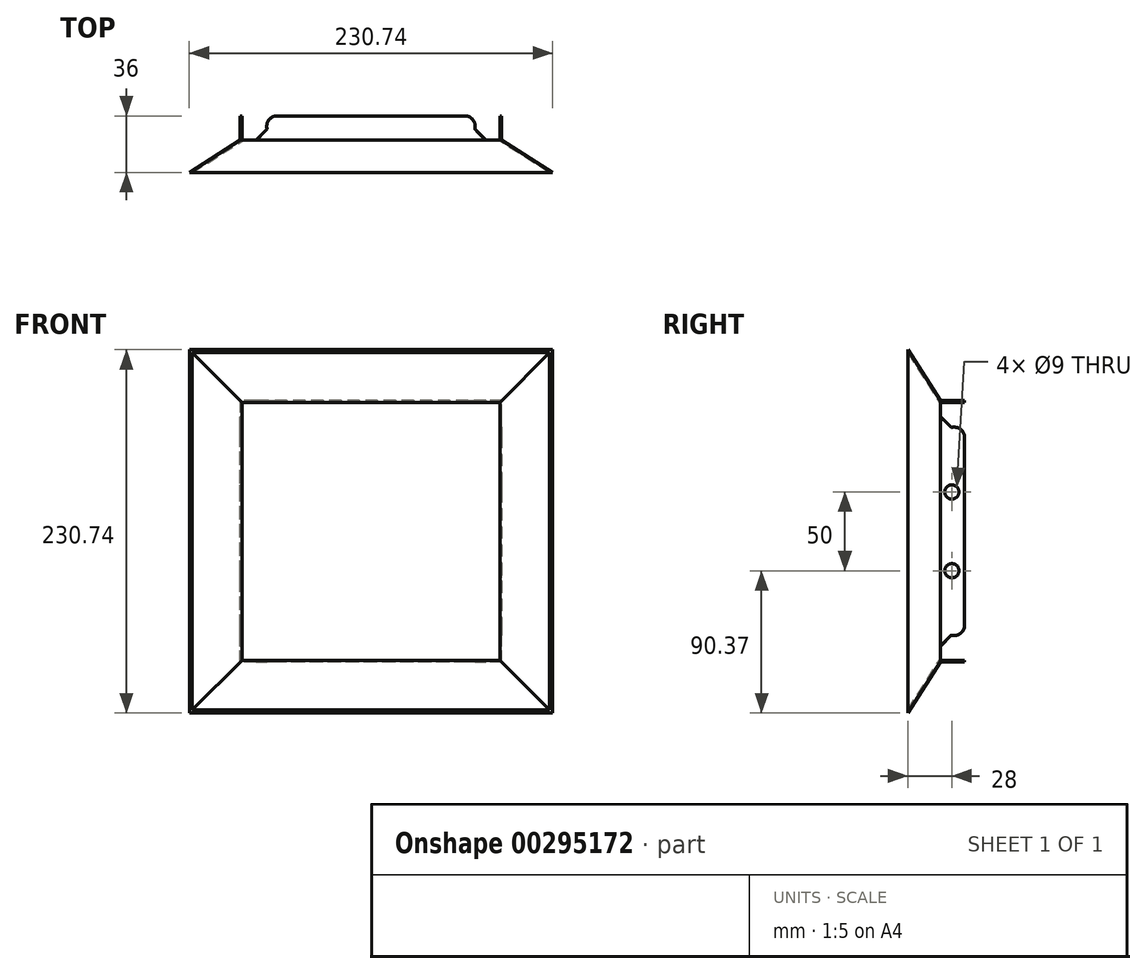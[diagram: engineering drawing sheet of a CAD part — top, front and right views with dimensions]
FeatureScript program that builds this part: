
annotation { "Feature Type Name" : "Feature", "Feature Type Description" : "" }
export const myFeature = defineFeature(function(context is Context, id is Id, definition is map)
    precondition{}
    {
        {
            var Q0;
            Q0=qCreatedBy(makeId("Front.planeOp"),FACE);
            var sketch = newSketch(context, id + "F0", { "sketchPlane" : qUnion([Q0])});
            skLineSegment(sketch, "E0.bottom", {"start": v(118.5, 118.5) * mm, "end": v(-118.5, 118.5) * mm});
            skLineSegment(sketch, "E0.top", {"start": v(118.5, -118.5) * mm, "end": v(-118.5, -118.5) * mm});
            skLineSegment(sketch, "E0.left", {"start": v(118.5, 118.5) * mm, "end": v(118.5, -118.5) * mm});
            skLineSegment(sketch, "E0.right", {"start": v(-118.5, 118.5) * mm, "end": v(-118.5, -118.5) * mm});
            skPoint(sketch, "E0.middle", {"position": v(0, 0) * mm});
            skLineSegment(sketch, "E1.bottom", {"start": v(-113.5, 113.5) * mm, "end": v(113.5, 113.5) * mm});
            skLineSegment(sketch, "E1.top", {"start": v(-113.5, -113.5) * mm, "end": v(113.5, -113.5) * mm});
            skLineSegment(sketch, "E1.left", {"start": v(-113.5, 113.5) * mm, "end": v(-113.5, -113.5) * mm});
            skLineSegment(sketch, "E1.right", {"start": v(113.5, 113.5) * mm, "end": v(113.5, -113.5) * mm});
            skSolve(sketch);
        }
        {
            var Q0;
            Q0=qCreatedBy(makeId("Front.planeOp"),FACE);
            cPlane(context, id + "F1", {"entities" : qUnion([Q0]), "cplaneType" : CPlaneType.OFFSET, "offset" : 20 * mm, "oppositeDirection" : true, "width" : 150 * mm, "height" : 150 * mm});
        }
        {
            var Q0;
            Q0=qCreatedBy(id+"F1.planeOp",FACE);
            var sketch = newSketch(context, id + "F2", { "sketchPlane" : qUnion([Q0])});
            skLineSegment(sketch, "E2.bottom", {"start": v(82, 82) * mm, "end": v(-82, 82) * mm});
            skLineSegment(sketch, "E2.top", {"start": v(82, -82) * mm, "end": v(-82, -82) * mm});
            skLineSegment(sketch, "E2.left", {"start": v(82, 82) * mm, "end": v(82, -82) * mm});
            skLineSegment(sketch, "E2.right", {"start": v(-82, 82) * mm, "end": v(-82, -82) * mm});
            skPoint(sketch, "E2.middle", {"position": v(0, 0) * mm});
            skSolve(sketch);
        }
        {
            var Q0;
            Q0=makeQuery(id+"F0.imprint","IMPRINT",FACE,{"disambiguationData":[TD([[makeQuery(id+"F0.imprint","IMPRINT",EDGE,{"derivedFrom":sQuery(id+"F0.wireOp",EDGE,"E1.bottom")}),-1.0]])]});
            var Q1;
            Q1=makeQuery(id+"F2.imprint","IMPRINT",FACE,{"disambiguationData":[TD([[makeQuery(id+"F2.imprint","IMPRINT",EDGE,{"derivedFrom":sQuery(id+"F2.wireOp",EDGE,"E2.bottom")}),1.0]])]});
            loft(context, id + "F3", {"sheetProfilesArray" : [{ "sheetProfileEntities" : qUnion([Q0]) }, { "sheetProfileEntities" : qUnion([Q1]) }]});
        }
        {
            var Q0;
            Q0=qCreatedBy(id+"F1.planeOp",FACE);
            cPlane(context, id + "F4", {"entities" : qUnion([Q0]), "cplaneType" : CPlaneType.OFFSET, "offset" : 16 * mm, "oppositeDirection" : true, "width" : 150 * mm, "height" : 150 * mm});
        }
        {
            var Q0;
            Q0=qCreatedBy(id+"F4.planeOp",FACE);
            var sketch = newSketch(context, id + "F5", { "sketchPlane" : qUnion([Q0])});
            skLineSegment(sketch, "E3.0.0", {"start": v(82, -82) * mm, "end": v(-82, -82) * mm});
            skLineSegment(sketch, "E3.0.1", {"start": v(-82, -82) * mm, "end": v(-82, 82) * mm});
            skLineSegment(sketch, "E3.0.2", {"start": v(-82, 82) * mm, "end": v(82, 82) * mm});
            skLineSegment(sketch, "E3.0.3", {"start": v(82, 82) * mm, "end": v(82, -82) * mm});
            skSolve(sketch);
        }
        {
            var Q1;
            Q1=makeQuery(id+"F5.imprint","IMPRINT",FACE,{"disambiguationData":[TD([[makeQuery(id+"F5.imprint","IMPRINT",EDGE,{"derivedFrom":sQuery(id+"F5.wireOp",EDGE,"E3.0.0")}),-1.0]])]});
            var Q2;
            Q2=makeQuery(id+"F3.opLoft","CAP_FACE",FACE,{"disambiguationData":[OSD([makeQuery(id+"F2.imprint","IMPRINT",FACE,{"disambiguationData":[TD([[makeQuery(id+"F2.imprint","IMPRINT",EDGE,{"derivedFrom":sQuery(id+"F2.wireOp",EDGE,"E2.bottom")}),1.0]])]})])],"isStart":true});
            loft(context, id + "F6", {"operationType" : NewBodyOperationType.ADD, "sheetProfilesArray" : [{ "sheetProfileEntities" : qUnion([Q1]) }, { "sheetProfileEntities" : qUnion([Q2]) }]});
        }
        {
            var Q0;
            Q0=makeQuery(id+"F3.opLoft","CAP_FACE",FACE,{"disambiguationData":[OSD([makeQuery(id+"F0.imprint","IMPRINT",FACE,{"disambiguationData":[TD([[makeQuery(id+"F0.imprint","IMPRINT",EDGE,{"derivedFrom":sQuery(id+"F0.wireOp",EDGE,"E1.bottom")}),-1.0]])]})])],"isStart":true});
            var Q1;
            Q1=makeQuery(id+"F6.opLoft","CAP_FACE",FACE,{"disambiguationData":[OSD([makeQuery(id+"F5.imprint","IMPRINT",FACE,{"disambiguationData":[TD([[makeQuery(id+"F5.imprint","IMPRINT",EDGE,{"derivedFrom":sQuery(id+"F5.wireOp",EDGE,"E3.0.0")}),-1.0]])]})])],"isStart":true});
            shell(context, id + "F7", {"entities" : qUnion([Q0, Q1]), "thickness" : 1 * mm, "oppositeDirection" : true});
        }
        {
            var Q0;
            Q0=makeQuery(id+"F6.opLoft","SWEPT_FACE",FACE,{"disambiguationData":[OSD([sQuery(id+"F2.wireOp",EDGE,"E2.bottom"),sQuery(id+"F2.wireOp",EDGE,"E2.top"),sQuery(id+"F2.wireOp",EDGE,"E2.right"),sQuery(id+"F5.wireOp",EDGE,"E3.0.0"),sQuery(id+"F5.wireOp",EDGE,"E3.0.1"),sQuery(id+"F5.wireOp",EDGE,"E3.0.2")])]});
            var sketch = newSketch(context, id + "F8", { "sketchPlane" : qUnion([Q0])});
            skLineSegment(sketch, "E4", {"start": v(-20.55, 83) * mm, "end": v(-20.55, 73) * mm});
            skLineSegment(sketch, "E5", {"start": v(-20.55, 73) * mm, "end": v(-27.62, 65.93) * mm});
            skArc(sketch, "E6", {"start": v(-27.62, 65.93) * mm, "mid": v(-33.79, 64.53) * mm, "end": v(-36, 58.6) * mm});
            skLineSegment(sketch, "E7", {"start": v(-20.55, 83) * mm, "end": v(-36, 83) * mm});
            skLineSegment(sketch, "E8", {"start": v(-36, 83) * mm, "end": v(-36, 58.6) * mm});
            skLineSegment(sketch, "E9.MirrorCS", {"start": v(-20.55, -83) * mm, "end": v(-36, -83) * mm});
            skArc(sketch, "E10.MirrorCS", {"start": v(-27.62, -65.93) * mm, "mid": v(-33.79, -64.53) * mm, "end": v(-36, -58.6) * mm});
            skLineSegment(sketch, "E11.MirrorCS", {"start": v(-20.55, -83) * mm, "end": v(-20.55, -73) * mm});
            skLineSegment(sketch, "E12.MirrorCS", {"start": v(-20.55, -73) * mm, "end": v(-27.62, -65.93) * mm});
            skLineSegment(sketch, "E13.MirrorCS", {"start": v(-36, -83) * mm, "end": v(-36, -58.6) * mm});
            skSolve(sketch);
        }
        {
            var Q0;
            Q0=makeQuery(id+"F8.imprint","IMPRINT",FACE,{"disambiguationData":[TD([[makeQuery(id+"F8.imprint","IMPRINT",EDGE,{"derivedFrom":sQuery(id+"F8.wireOp",EDGE,"E4")}),1.0]])]});
            var Q1;
            Q1=sQuery(id+"F8.wireOp",EDGE,"E7");
            revolve(context, id + "F9", {"operationType" : NewBodyOperationType.REMOVE, "entities" : qUnion([Q0]), "axis" : qUnion([Q1]), "revolveType" : RevolveType.FULL, "oppositeDirection" : true});
        }
        {
            var Q0;
            {var subQ4=sQuery(id+"F8.wireOp",EDGE,"E9.MirrorCS");Q0=makeQuery(id+"F8.imprint","IMPRINT",FACE,{"disambiguationData":[TD([[makeQuery(id+"F8.imprint","IMPRINT",EDGE,{"derivedFrom":subQ4}),1.0]])]});}
            var Q1;
            Q1=sQuery(id+"F8.wireOp",EDGE,"E9.MirrorCS");
            revolve(context, id + "F10", {"operationType" : NewBodyOperationType.REMOVE, "entities" : qUnion([Q0]), "axis" : qUnion([Q1]), "revolveType" : RevolveType.FULL, "oppositeDirection" : true});
        }
        {
            var Q0;
            Q0=makeQuery(id+"F6.opLoft","SWEPT_FACE",FACE,{"disambiguationData":[OSD([sQuery(id+"F2.wireOp",EDGE,"E2.bottom"),sQuery(id+"F2.wireOp",EDGE,"E2.top"),sQuery(id+"F2.wireOp",EDGE,"E2.left"),sQuery(id+"F5.wireOp",EDGE,"E3.0.0"),sQuery(id+"F5.wireOp",EDGE,"E3.0.2"),sQuery(id+"F5.wireOp",EDGE,"E3.0.3")])]});
            var sketch = newSketch(context, id + "F11", { "sketchPlane" : qUnion([Q0])});
            skLineSegment(sketch, "E14.0", {"start": v(20.55, -73) * mm, "end": v(27.62, -65.93) * mm});
            skArc(sketch, "E15.0", {"start": v(27.62, -65.93) * mm, "mid": v(33.79, -64.53) * mm, "end": v(36, -58.6) * mm});
            skLineSegment(sketch, "E16.0", {"start": v(20.55, -83) * mm, "end": v(20.55, -73) * mm});
            skLineSegment(sketch, "E17.0", {"start": v(20.55, -83) * mm, "end": v(36, -83) * mm});
            skLineSegment(sketch, "E18.0", {"start": v(36, -83) * mm, "end": v(36, -58.6) * mm});
            skLineSegment(sketch, "E19.MirrorCS", {"start": v(20.55, 83) * mm, "end": v(20.55, 73) * mm});
            skLineSegment(sketch, "E20.MirrorCS", {"start": v(20.55, 83) * mm, "end": v(36, 83) * mm});
            skLineSegment(sketch, "E21.MirrorCS", {"start": v(20.55, 73) * mm, "end": v(27.62, 65.93) * mm});
            skLineSegment(sketch, "E22.MirrorCS", {"start": v(36, 83) * mm, "end": v(36, 58.6) * mm});
            skArc(sketch, "E23.MirrorCS", {"start": v(27.62, 65.93) * mm, "mid": v(33.79, 64.53) * mm, "end": v(36, 58.6) * mm});
            skSolve(sketch);
        }
        {
            var Q0;
            {var subQ2=sQuery(id+"F11.wireOp",EDGE,"E14.0");Q0=makeQuery(id+"F11.imprint","IMPRINT",FACE,{"disambiguationData":[TD([[makeQuery(id+"F11.imprint","IMPRINT",EDGE,{"derivedFrom":subQ2}),-1.0]])]});}
            var Q1;
            Q1=sQuery(id+"F11.wireOp",EDGE,"E17.0");
            revolve(context, id + "F12", {"operationType" : NewBodyOperationType.REMOVE, "entities" : qUnion([Q0]), "axis" : qUnion([Q1]), "revolveType" : RevolveType.FULL, "oppositeDirection" : true});
        }
        {
            var Q0;
            Q0=makeQuery(id+"F11.imprint","IMPRINT",FACE,{"disambiguationData":[TD([[makeQuery(id+"F11.imprint","IMPRINT",EDGE,{"derivedFrom":sQuery(id+"F11.wireOp",EDGE,"E19.MirrorCS")}),1.0]])]});
            var Q1;
            Q1=sQuery(id+"F11.wireOp",EDGE,"E20.MirrorCS");
            revolve(context, id + "F13", {"operationType" : NewBodyOperationType.REMOVE, "entities" : qUnion([Q0]), "axis" : qUnion([Q1]), "revolveType" : RevolveType.FULL, "oppositeDirection" : true});
        }
        {
            var Q0;
            {var subQ2=sQuery(id+"F11.wireOp",EDGE,"E14.0");Q0=makeQuery(id+"F11.imprint","IMPRINT",FACE,{"disambiguationData":[TD([[makeQuery(id+"F11.imprint","IMPRINT",EDGE,{"derivedFrom":subQ2}),1.0]])]});}
            var sketch = newSketch(context, id + "F14", { "sketchPlane" : qUnion([Q0])});
            skCircle(sketch, "E24", {"center": v(28, 25) * mm, "radius": 4.5 * mm});
            skCircle(sketch, "E25", {"center": v(28, -25) * mm, "radius": 4.5 * mm});
            skSolve(sketch);
        }
        {
            var Q0;
            Q0 = qSketchRegion(id + "F14", true);
            extrude(context, id + "F15", {"entities" : qUnion([Q0]), "operationType" : NewBodyOperationType.REMOVE, "endBound" : BoundingType.THROUGH_ALL, "oppositeDirection" : true, "depth" : 25 * mm});
        }
    });
